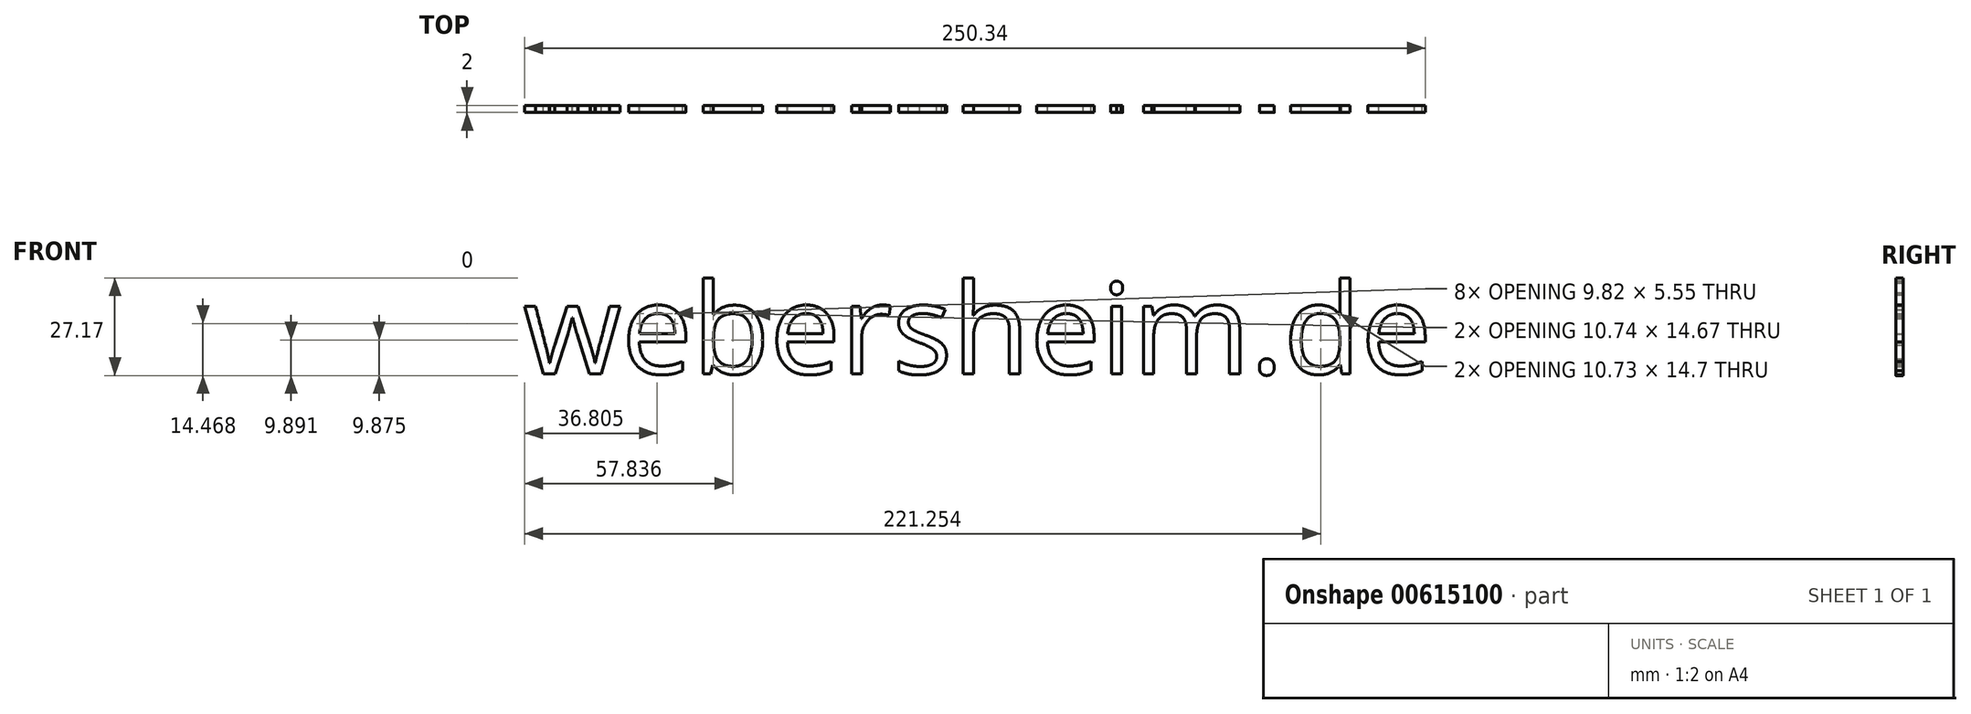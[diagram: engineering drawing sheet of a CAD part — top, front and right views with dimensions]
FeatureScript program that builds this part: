
annotation { "Feature Type Name" : "Feature", "Feature Type Description" : "" }
export const myFeature = defineFeature(function(context is Context, id is Id, definition is map)
    precondition{}
    {
        {
            var Q0;
            Q0=qCreatedBy(makeId("Front.planeOp"),FACE);
            var sketch = newSketch(context, id + "F0", { "sketchPlane" : qUnion([Q0])});
            skText(sketch, "E0", { "text": "webersheim.de", "fontName": "OpenSans-Regular.ttf"});
            const initialGuessF0  = {"E0": [-0.06057, 0.01074, 1, 0, 0.02527]};
            skSetInitialGuess(sketch, initialGuessF0);
            skSolve(sketch);
        }
        {
            var Q0;
            Q0 = qSketchRegion(id + "F0", true);
            extrude(context, id + "F1", {"entities" : qUnion([Q0]), "depth" : 2 * mm, "offsetDistance" : 25.4 * mm});
        }
    });
